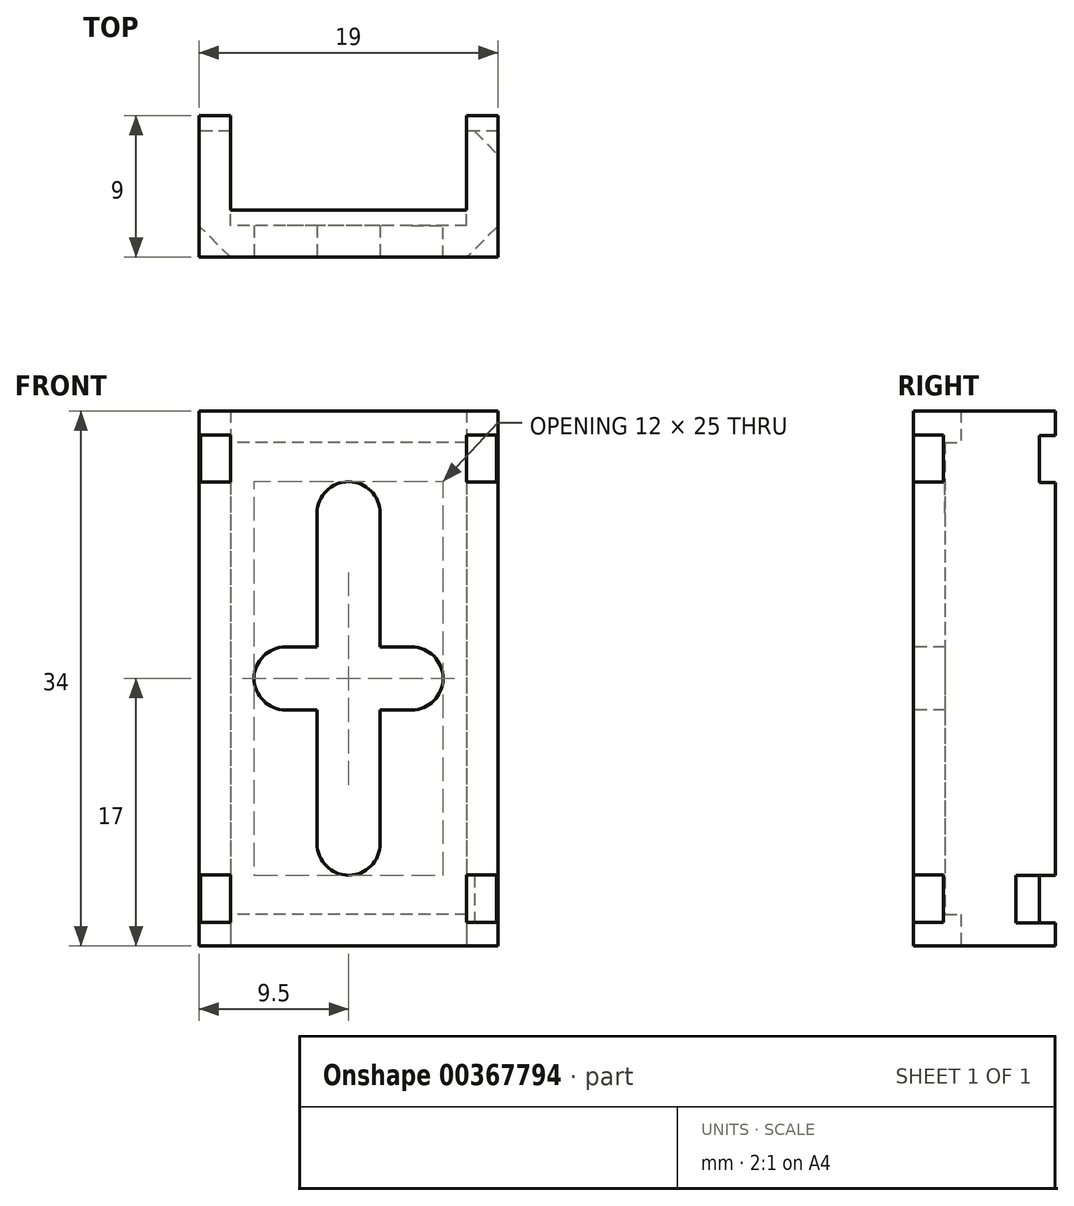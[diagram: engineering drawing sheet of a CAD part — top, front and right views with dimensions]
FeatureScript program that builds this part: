
annotation { "Feature Type Name" : "Feature", "Feature Type Description" : "" }
export const myFeature = defineFeature(function(context is Context, id is Id, definition is map)
    precondition{}
    {
        {
            var Q0;
            Q0=qCreatedBy(makeId("Front.planeOp"),FACE);
            var sketch = newSketch(context, id + "F0", { "sketchPlane" : qUnion([Q0])});
            skLineSegment(sketch, "E0.bottom", {"start": v(9.5, 17) * mm, "end": v(-9.5, 17) * mm});
            skLineSegment(sketch, "E0.top", {"start": v(9.5, -17) * mm, "end": v(-9.5, -17) * mm});
            skLineSegment(sketch, "E0.left", {"start": v(9.5, 17) * mm, "end": v(9.5, -17) * mm});
            skLineSegment(sketch, "E0.right", {"start": v(-9.5, 17) * mm, "end": v(-9.5, -17) * mm});
            skPoint(sketch, "E0.middle", {"position": v(0, 0) * mm});
            skSolve(sketch);
        }
        {
            var Q0;
            Q0 = qSketchRegion(id + "F0", true);
            extrude(context, id + "F1", {"entities" : qUnion([Q0]), "depth" : 9 * mm});
        }
        {
            var Q0;
            Q0=makeQuery(id+"F1.opExtrude","CAP_FACE",FACE,{"disambiguationData":[OSD([sQuery(id+"F0.wireOp",EDGE,"E0.bottom"),sQuery(id+"F0.wireOp",EDGE,"E0.top"),sQuery(id+"F0.wireOp",EDGE,"E0.left"),sQuery(id+"F0.wireOp",EDGE,"E0.right")])],"isStart":true});
            shell(context, id + "F2", {"entities" : qUnion([Q0]), "thickness" : 2 * mm});
        }
        {
            var Q0;
            Q0=makeQuery(id+"F1.opExtrude","CAP_FACE",FACE,{"disambiguationData":[OSD([sQuery(id+"F0.wireOp",EDGE,"E0.bottom"),sQuery(id+"F0.wireOp",EDGE,"E0.top"),sQuery(id+"F0.wireOp",EDGE,"E0.left"),sQuery(id+"F0.wireOp",EDGE,"E0.right")])],"isStart":true});
            var sketch = newSketch(context, id + "F3", { "sketchPlane" : qUnion([Q0])});
            skPoint(sketch, "E1", {"position": v(-7.5, 17) * mm});
            skPoint(sketch, "E2", {"position": v(7.5, 17) * mm});
            skPoint(sketch, "E3", {"position": v(7.5, -17) * mm});
            skPoint(sketch, "E4", {"position": v(-7.5, -17) * mm});
            skLineSegment(sketch, "E5.bottom", {"start": v(-7.5, 17) * mm, "end": v(7.5, 17) * mm});
            skLineSegment(sketch, "E5.top", {"start": v(-7.5, -17) * mm, "end": v(7.5, -17) * mm});
            skLineSegment(sketch, "E5.left", {"start": v(-7.5, 17) * mm, "end": v(-7.5, -17) * mm});
            skLineSegment(sketch, "E5.right", {"start": v(7.5, 17) * mm, "end": v(7.5, -17) * mm});
            skSolve(sketch);
        }
        {
            var Q0;
            Q0 = qSketchRegion(id + "F3", true);
            extrude(context, id + "F4", {"entities" : qUnion([Q0]), "operationType" : NewBodyOperationType.REMOVE, "oppositeDirection" : true, "depth" : 6 * mm});
        }
        {
            var Q0;
            Q0=makeQuery(id+"F1.opExtrude","CAP_FACE",FACE,{"disambiguationData":[OSD([sQuery(id+"F0.wireOp",EDGE,"E0.bottom"),sQuery(id+"F0.wireOp",EDGE,"E0.top"),sQuery(id+"F0.wireOp",EDGE,"E0.left"),sQuery(id+"F0.wireOp",EDGE,"E0.right")])],"isStart":false});
            var sketch = newSketch(context, id + "F5", { "sketchPlane" : qUnion([Q0])});
            skLineSegment(sketch, "E6.bottom", {"start": v(2, 12.5) * mm, "end": v(-2, 12.5) * mm});
            skLineSegment(sketch, "E6.top", {"start": v(2, -12.5) * mm, "end": v(-2, -12.5) * mm});
            skLineSegment(sketch, "E6.left", {"start": v(2, 12.5) * mm, "end": v(2, -12.5) * mm});
            skLineSegment(sketch, "E6.right", {"start": v(-2, 12.5) * mm, "end": v(-2, -12.5) * mm});
            skPoint(sketch, "E6.middle", {"position": v(0, 0) * mm});
            skLineSegment(sketch, "E7.bottom", {"start": v(6, -2) * mm, "end": v(-6, -2) * mm});
            skLineSegment(sketch, "E7.top", {"start": v(6, 2) * mm, "end": v(-6, 2) * mm});
            skLineSegment(sketch, "E7.left", {"start": v(6, -2) * mm, "end": v(6, 2) * mm});
            skLineSegment(sketch, "E7.right", {"start": v(-6, -2) * mm, "end": v(-6, 2) * mm});
            skSolve(sketch);
        }
        {
            var Q0;
            Q0 = qSketchRegion(id + "F5", true);
            extrude(context, id + "F6", {"entities" : qUnion([Q0]), "operationType" : NewBodyOperationType.REMOVE, "oppositeDirection" : true, "depth" : 10 * mm});
        }
        {
            var Q0;
            Q0=makeQuery(id+"F6.boolean.opBoolean","COPY",EDGE,{"derivedFrom":makeQuery(id+"F6.opExtrude","SWEPT_EDGE",EDGE,{"disambiguationData":[OSD([sQuery(id+"F5.wireOp",EDGE,"E6.bottom"),sQuery(id+"F5.wireOp",EDGE,"E6.left")])]})});
            var Q1;
            Q1=makeQuery(id+"F6.boolean.opBoolean","COPY",EDGE,{"derivedFrom":makeQuery(id+"F6.opExtrude","SWEPT_EDGE",EDGE,{"disambiguationData":[OSD([sQuery(id+"F5.wireOp",EDGE,"E6.bottom"),sQuery(id+"F5.wireOp",EDGE,"E6.right")])]})});
            var Q2;
            Q2=makeQuery(id+"F6.boolean.opBoolean","COPY",EDGE,{"derivedFrom":makeQuery(id+"F6.opExtrude","SWEPT_EDGE",EDGE,{"disambiguationData":[OSD([sQuery(id+"F5.wireOp",EDGE,"E7.top"),sQuery(id+"F5.wireOp",EDGE,"E7.right")])]})});
            var Q3;
            Q3=makeQuery(id+"F6.boolean.opBoolean","COPY",EDGE,{"derivedFrom":makeQuery(id+"F6.opExtrude","SWEPT_EDGE",EDGE,{"disambiguationData":[OSD([sQuery(id+"F5.wireOp",EDGE,"E7.top"),sQuery(id+"F5.wireOp",EDGE,"E7.left")])]})});
            var Q4;
            Q4=makeQuery(id+"F6.boolean.opBoolean","COPY",EDGE,{"derivedFrom":makeQuery(id+"F6.opExtrude","SWEPT_EDGE",EDGE,{"disambiguationData":[OSD([sQuery(id+"F5.wireOp",EDGE,"E7.bottom"),sQuery(id+"F5.wireOp",EDGE,"E7.right")])]})});
            var Q5;
            Q5=makeQuery(id+"F6.boolean.opBoolean","COPY",EDGE,{"derivedFrom":makeQuery(id+"F6.opExtrude","SWEPT_EDGE",EDGE,{"disambiguationData":[OSD([sQuery(id+"F5.wireOp",EDGE,"E7.bottom"),sQuery(id+"F5.wireOp",EDGE,"E7.left")])]})});
            var Q6;
            Q6=makeQuery(id+"F6.boolean.opBoolean","COPY",EDGE,{"derivedFrom":makeQuery(id+"F6.opExtrude","SWEPT_EDGE",EDGE,{"disambiguationData":[OSD([sQuery(id+"F5.wireOp",EDGE,"E6.top"),sQuery(id+"F5.wireOp",EDGE,"E6.right")])]})});
            var Q7;
            Q7=makeQuery(id+"F6.boolean.opBoolean","COPY",EDGE,{"derivedFrom":makeQuery(id+"F6.opExtrude","SWEPT_EDGE",EDGE,{"disambiguationData":[OSD([sQuery(id+"F5.wireOp",EDGE,"E6.top"),sQuery(id+"F5.wireOp",EDGE,"E6.left")])]})});
            fillet(context, id + "F7", {"entities" : qUnion([Q0, Q1, Q2, Q3, Q4, Q5, Q6, Q7]), "radius" : 2 * mm, "tangentPropagation" : true, "allowEdgeOverflow" : false});
        }
        {
            var Q0;
            Q0=makeQuery(id+"F1.opExtrude","CAP_FACE",FACE,{"disambiguationData":[OSD([sQuery(id+"F0.wireOp",EDGE,"E0.bottom"),sQuery(id+"F0.wireOp",EDGE,"E0.top"),sQuery(id+"F0.wireOp",EDGE,"E0.left"),sQuery(id+"F0.wireOp",EDGE,"E0.right")])],"isStart":false});
            var sketch = newSketch(context, id + "F8", { "sketchPlane" : qUnion([Q0])});
            skLineSegment(sketch, "E8.bottom", {"start": v(-9.5, 12.46) * mm, "end": v(9.5, 12.46) * mm});
            skLineSegment(sketch, "E8.top", {"start": v(-9.5, 15.46) * mm, "end": v(9.5, 15.46) * mm});
            skLineSegment(sketch, "E8.left", {"start": v(-9.5, 12.46) * mm, "end": v(-9.5, 15.46) * mm});
            skLineSegment(sketch, "E8.right", {"start": v(9.5, 12.46) * mm, "end": v(9.5, 15.46) * mm});
            skLineSegment(sketch, "E9.bottom", {"start": v(-9.5, -12.5) * mm, "end": v(9.5, -12.5) * mm});
            skLineSegment(sketch, "E9.top", {"start": v(-9.5, -15.5) * mm, "end": v(9.5, -15.5) * mm});
            skLineSegment(sketch, "E9.left", {"start": v(-9.5, -12.5) * mm, "end": v(-9.5, -15.5) * mm});
            skLineSegment(sketch, "E9.right", {"start": v(9.5, -12.5) * mm, "end": v(9.5, -15.5) * mm});
            skLineSegment(sketch, "E10.bottom", {"start": v(-7.5, 15.46) * mm, "end": v(7.5, 15.46) * mm});
            skLineSegment(sketch, "E10.top", {"start": v(-7.5, -15.5) * mm, "end": v(7.5, -15.5) * mm});
            skLineSegment(sketch, "E10.left", {"start": v(-7.5, 15.46) * mm, "end": v(-7.5, -15.5) * mm});
            skLineSegment(sketch, "E10.right", {"start": v(7.5, 15.46) * mm, "end": v(7.5, -15.5) * mm});
            skSolve(sketch);
        }
        {
            var Q0;
            {var subQ0=sQuery(id+"F8.wireOp",EDGE,"E9.left");Q0=makeQuery(id+"F8.imprint","IMPRINT",FACE,{"disambiguationData":[TD([[makeQuery(id+"F8.imprint","IMPRINT",EDGE,{"derivedFrom":subQ0}),1.0]])]});}
            var Q1;
            {var subQ0=sQuery(id+"F8.wireOp",EDGE,"E8.right");Q1=makeQuery(id+"F8.imprint","IMPRINT",FACE,{"disambiguationData":[TD([[makeQuery(id+"F8.imprint","IMPRINT",EDGE,{"derivedFrom":subQ0}),-1.0]])]});}
            var Q2;
            {var subQ0=sQuery(id+"F8.wireOp",EDGE,"E8.left");Q2=makeQuery(id+"F8.imprint","IMPRINT",FACE,{"disambiguationData":[TD([[makeQuery(id+"F8.imprint","IMPRINT",EDGE,{"derivedFrom":subQ0}),1.0]])]});}
            var Q3;
            {var subQ0=sQuery(id+"F8.wireOp",EDGE,"E9.right");Q3=makeQuery(id+"F8.imprint","IMPRINT",FACE,{"disambiguationData":[TD([[makeQuery(id+"F8.imprint","IMPRINT",EDGE,{"derivedFrom":subQ0}),-1.0]])]});}
            extrude(context, id + "F9", {"entities" : qUnion([Q0, Q1, Q2, Q3]), "operationType" : NewBodyOperationType.REMOVE, "oppositeDirection" : true, "depth" : 1.9 * mm});
        }
        {
            var Q0;
            {var subQ0=sQuery(id+"F8.wireOp",EDGE,"E10.right");Q0=makeQuery(id+"F9.boolean.opBoolean","COPY",EDGE,{"derivedFrom":makeQuery(id+"F9.opExtrude","CAP_EDGE",EDGE,{"disambiguationData":[OSD([subQ0]),TDD([makeQuery(id+"F8.imprint","IMPRINT",EDGE,{"disambiguationData":[TD([[makeQuery(id+"F8.imprint","INTERSECT",VERTEX,{"derivedFrom":[sQuery(id+"F8.wireOp",EDGE,"E8.bottom"),subQ0]}),1.0]])],"derivedFrom":subQ0})])],"isStart":false})});}
            var Q1;
            {var subQ0=sQuery(id+"F8.wireOp",EDGE,"E10.left");Q1=makeQuery(id+"F9.boolean.opBoolean","COPY",EDGE,{"derivedFrom":makeQuery(id+"F9.opExtrude","CAP_EDGE",EDGE,{"disambiguationData":[OSD([subQ0]),TDD([makeQuery(id+"F8.imprint","IMPRINT",EDGE,{"disambiguationData":[TD([[makeQuery(id+"F8.imprint","INTERSECT",VERTEX,{"derivedFrom":[sQuery(id+"F8.wireOp",EDGE,"E8.bottom"),subQ0]}),1.0]])],"derivedFrom":subQ0})])],"isStart":false})});}
            var Q2;
            {var subQ0=sQuery(id+"F8.wireOp",EDGE,"E10.left");Q2=makeQuery(id+"F9.boolean.opBoolean","COPY",EDGE,{"derivedFrom":makeQuery(id+"F9.opExtrude","CAP_EDGE",EDGE,{"disambiguationData":[OSD([subQ0]),TDD([makeQuery(id+"F8.imprint","IMPRINT",EDGE,{"disambiguationData":[TD([[makeQuery(id+"F8.imprint","INTERSECT",VERTEX,{"derivedFrom":[sQuery(id+"F8.wireOp",EDGE,"E9.bottom"),subQ0]}),-1.0]])],"derivedFrom":subQ0})])],"isStart":false})});}
            var Q3;
            {var subQ0=sQuery(id+"F8.wireOp",EDGE,"E10.right");Q3=makeQuery(id+"F9.boolean.opBoolean","COPY",EDGE,{"derivedFrom":makeQuery(id+"F9.opExtrude","CAP_EDGE",EDGE,{"disambiguationData":[OSD([subQ0]),TDD([makeQuery(id+"F8.imprint","IMPRINT",EDGE,{"disambiguationData":[TD([[makeQuery(id+"F8.imprint","INTERSECT",VERTEX,{"derivedFrom":[sQuery(id+"F8.wireOp",EDGE,"E9.bottom"),subQ0]}),-1.0]])],"derivedFrom":subQ0})])],"isStart":false})});}
            chamfer(context, id + "F10", {"entities" : qUnion([Q0, Q1, Q2, Q3]), "width" : 1.9 * mm, "tangentPropagation" : true});
        }
        {
            var Q0;
            {var subQ0=sQuery(id+"F0.wireOp",EDGE,"E0.top");var subQ1=sQuery(id+"F0.wireOp",EDGE,"E0.right");var subQ2=sQuery(id+"F0.wireOp",EDGE,"E0.bottom");Q0=makeQuery(id+"F4.boolean.opBoolean","SPLIT",FACE,{"disambiguationData":[TD([makeQuery(id+"F1.opExtrude","SWEPT_FACE",FACE,{"disambiguationData":[OSD([subQ1])]})])],"derivedFrom":makeQuery(id+"F1.opExtrude","CAP_FACE",FACE,{"disambiguationData":[OSD([subQ2,subQ0,sQuery(id+"F0.wireOp",EDGE,"E0.left"),subQ1])],"isStart":true})});}
            var sketch = newSketch(context, id + "F11", { "sketchPlane" : qUnion([Q0])});
            skLineSegment(sketch, "E11.bottom", {"start": v(-9.5, 12.43) * mm, "end": v(9.5, 12.43) * mm});
            skLineSegment(sketch, "E11.top", {"start": v(-9.5, 15.43) * mm, "end": v(9.5, 15.43) * mm});
            skLineSegment(sketch, "E11.left", {"start": v(-9.5, 12.43) * mm, "end": v(-9.5, 15.43) * mm});
            skLineSegment(sketch, "E11.right", {"start": v(9.5, 12.43) * mm, "end": v(9.5, 15.43) * mm});
            skLineSegment(sketch, "E12.bottom", {"start": v(-9.93, -12.51) * mm, "end": v(9.5, -12.51) * mm});
            skLineSegment(sketch, "E12.top", {"start": v(-9.93, -15.51) * mm, "end": v(9.5, -15.51) * mm});
            skLineSegment(sketch, "E12.left", {"start": v(-9.93, -12.51) * mm, "end": v(-9.93, -15.51) * mm});
            skLineSegment(sketch, "E12.right", {"start": v(9.5, -12.51) * mm, "end": v(9.5, -15.51) * mm});
            skLineSegment(sketch, "E13.bottom", {"start": v(-7.5, 15.43) * mm, "end": v(7.5, 15.43) * mm});
            skLineSegment(sketch, "E13.top", {"start": v(-7.5, -15.51) * mm, "end": v(7.5, -15.51) * mm});
            skLineSegment(sketch, "E13.left", {"start": v(-7.5, 15.43) * mm, "end": v(-7.5, -15.51) * mm});
            skLineSegment(sketch, "E13.right", {"start": v(7.5, 15.43) * mm, "end": v(7.5, -15.51) * mm});
            skSolve(sketch);
        }
        {
            var Q0;
            {var subQ0=sQuery(id+"F11.wireOp",EDGE,"E11.left");Q0=makeQuery(id+"F11.imprint","IMPRINT",FACE,{"disambiguationData":[TD([[makeQuery(id+"F11.imprint","IMPRINT",EDGE,{"derivedFrom":subQ0}),-1.0]])]});}
            var Q1;
            {var subQ0=sQuery(id+"F11.wireOp",EDGE,"E13.right");var subQ1=sQuery(id+"F11.wireOp",EDGE,"E11.bottom");var subQ2=makeQuery(id+"F11.imprint","INTERSECT",VERTEX,{"derivedFrom":[subQ1,subQ0]});Q1=makeQuery(id+"F11.imprint","IMPRINT",FACE,{"disambiguationData":[TD([[makeQuery(id+"F11.imprint","IMPRINT",EDGE,{"disambiguationData":[TD([[subQ2,-1.0]])],"derivedFrom":subQ1}),1.0]])]});}
            var Q2;
            {var subQ0=sQuery(id+"F11.wireOp",EDGE,"E13.right");var subQ1=sQuery(id+"F11.wireOp",EDGE,"E12.bottom");var subQ2=makeQuery(id+"F11.imprint","INTERSECT",VERTEX,{"derivedFrom":[subQ1,subQ0]});Q2=makeQuery(id+"F11.imprint","IMPRINT",FACE,{"disambiguationData":[TD([[makeQuery(id+"F11.imprint","IMPRINT",EDGE,{"disambiguationData":[TD([[subQ2,-1.0]])],"derivedFrom":subQ1}),-1.0]])]});}
            var Q3;
            {var subQ0=sQuery(id+"F11.wireOp",EDGE,"E12.left");Q3=makeQuery(id+"F11.imprint","IMPRINT",FACE,{"disambiguationData":[TD([[makeQuery(id+"F11.imprint","IMPRINT",EDGE,{"derivedFrom":subQ0}),1.0]])]});}
            extrude(context, id + "F12", {"entities" : qUnion([Q0, Q1, Q2, Q3]), "operationType" : NewBodyOperationType.REMOVE, "oppositeDirection" : true, "depth" : 1 * mm});
        }
        {
            var Q0;
            Q0=makeQuery(id+"F12.boolean.opBoolean","INTERSECT",EDGE,{"derivedFrom":[makeQuery(id+"F1.opExtrude","SWEPT_FACE",FACE,{"disambiguationData":[OSD([sQuery(id+"F0.wireOp",EDGE,"E0.left")])]}),makeQuery(id+"F12.opExtrude","CAP_FACE",FACE,{"disambiguationData":[OSD([sQuery(id+"F11.wireOp",EDGE,"E12.bottom"),sQuery(id+"F11.wireOp",EDGE,"E12.top"),sQuery(id+"F11.wireOp",EDGE,"E12.left"),sQuery(id+"F11.wireOp",EDGE,"E13.left")])],"isStart":false})]});
            var Q1;
            Q1=makeQuery(id+"F12.boolean.opBoolean","COPY",EDGE,{"derivedFrom":makeQuery(id+"F12.opExtrude","CAP_EDGE",EDGE,{"disambiguationData":[OSD([sQuery(id+"F11.wireOp",EDGE,"E12.right")])],"isStart":false})});
            var Q2;
            Q2=makeQuery(id+"F12.boolean.opBoolean","COPY",EDGE,{"derivedFrom":makeQuery(id+"F12.opExtrude","CAP_EDGE",EDGE,{"disambiguationData":[OSD([sQuery(id+"F11.wireOp",EDGE,"E11.left")])],"isStart":false})});
            var Q3;
            Q3=makeQuery(id+"F12.boolean.opBoolean","COPY",EDGE,{"derivedFrom":makeQuery(id+"F12.opExtrude","CAP_EDGE",EDGE,{"disambiguationData":[OSD([sQuery(id+"F11.wireOp",EDGE,"E11.right")])],"isStart":false})});
            chamfer(context, id + "F13", {"entities" : qUnion([Q0, Q1, Q2, Q3]), "width" : 1.5 * mm, "tangentPropagation" : true});
        }
    });
